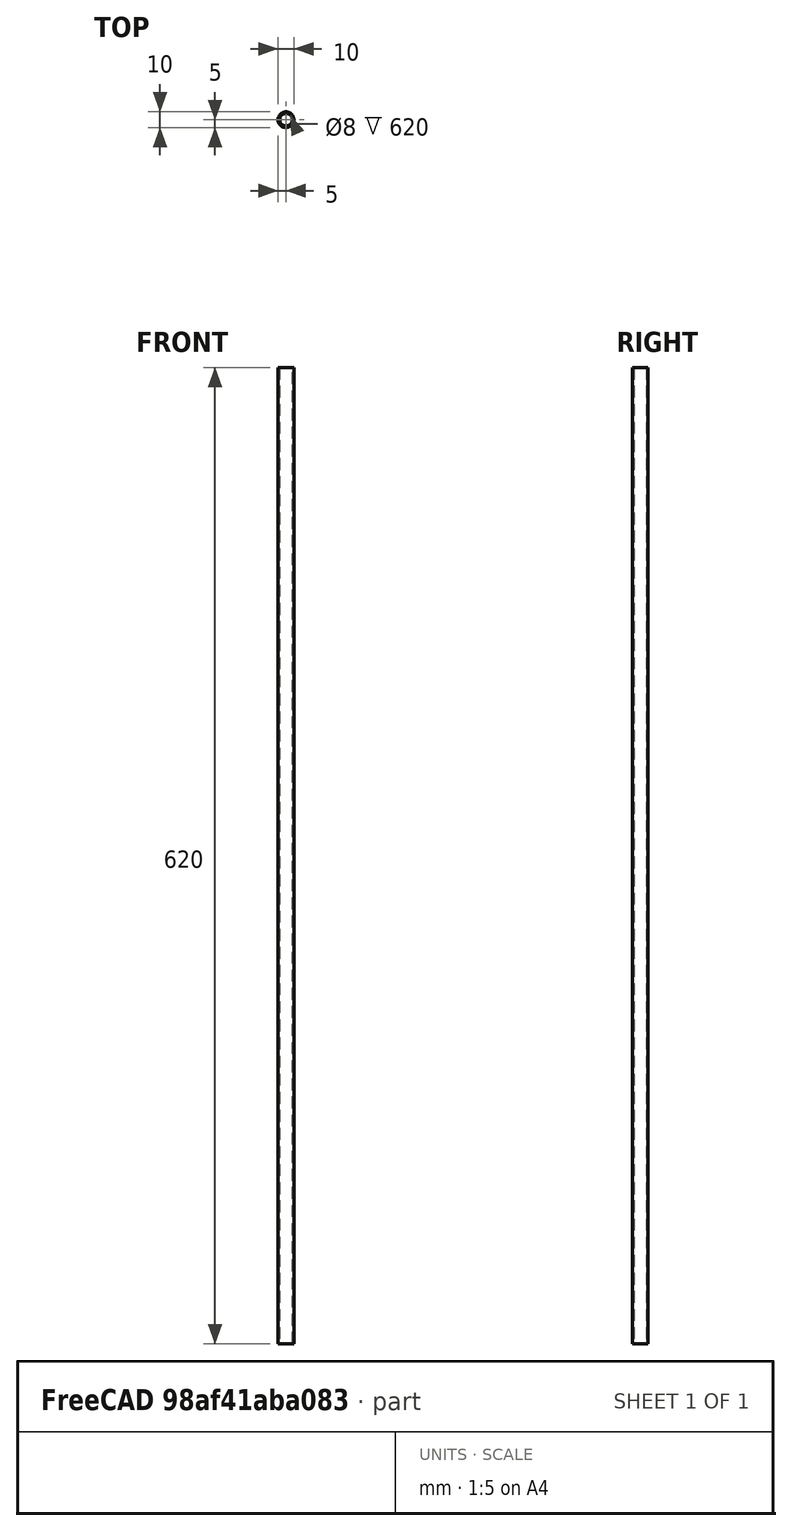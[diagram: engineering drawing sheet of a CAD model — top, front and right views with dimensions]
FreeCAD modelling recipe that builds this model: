
FCSTD DOCUMENT  (FreeCAD 0.19R16442 (Git))
Label: 10mm_rod
License: All rights reserved
LicenseURL: http://en.wikipedia.org/wiki/All_rights_reserved
objects: Sketcher::SketchObject×1, PartDesign::Pad×1, PartDesign::Body×1, App::Part×1
note: 4 computed .brp shape members not serialized (recipe doc carries the construction recipe); baked Part::Feature solids carry a one-line shape summary decoded from their .brp

FEATURE [Sketcher::SketchObject] Sketch
  MapMode = 5
  Support = -> [XY_Plane001]
  expr: Constraints[4] = Sketch.Constraints.outer_diameter - 2mm
  sketch-geometry (2):
    g0: Circle CenterX=0 CenterY=0 CenterZ=0 NormalX=0 NormalY=0 NormalZ=1 AngleXU=0 Radius=4
    g1: Circle CenterX=0 CenterY=0 CenterZ=0 NormalX=0 NormalY=0 NormalZ=1 AngleXU=0 Radius=5
  constraints (5):
    c: Coincident(g0,g-1)
    c: Coincident(g1,g0)
    c: Diameter(g1) = 10
    c: Diameter(g1) = 10  'outer_diameter'
    c: Diameter(g0) = 8
FEATURE [PartDesign::Pad] Pad
  Length = 620
  Length2 = 100
  Profile = -> Sketch
  Type = 0
FEATURE [PartDesign::Body] Body
  Group = -> [Sketch,Pad]
  Origin = -> Origin001
  Tip = -> Pad
FEATURE [App::Part] Part
  Group = -> [Body]
  Origin = -> Origin
